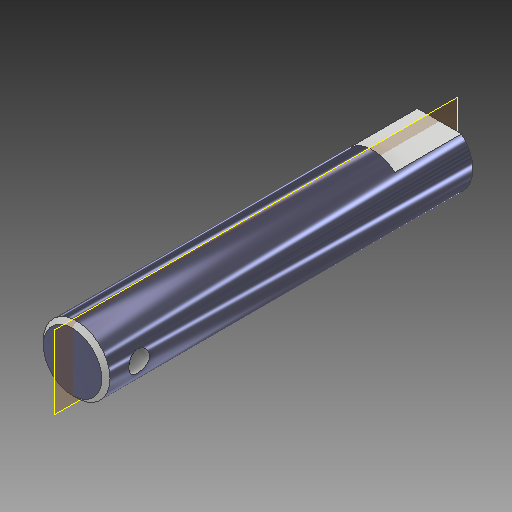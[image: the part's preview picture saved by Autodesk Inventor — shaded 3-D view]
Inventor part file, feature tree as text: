
AUTODESK INVENTOR PART (.ipt)
format: ipt  version: 2017 (Build 210142000, 142)  size: 155,648 bytes
history: native  units: mm
features: extrude x3, sketch x3, chamfer x1, plane x1
ambient origin geometry x8: Origin, YZ Plane, XZ Plane, XY Plane, X Axis, Y Axis, Z Axis, Center Point
bodies: Solid1 (feature_tree)
feature tree (8):
  extrude  "Extrusion1"  Depth=44.0mm TaperAngle=0.0deg
  chamfer  "Chamfer1"  Distance=0.5mm Angle=45.0deg
  extrude  "Extrusion2"  Depth=4.0mm
  plane  "Work Plane1"
  extrude  "Extrusion3"  Depth=4.0mm
  sketch  "Sketch2"  dims[d9=8.0mm d10=44.0mm d11=0.0mm d12=0.5mm d13=2.0mm d14=45.0deg]
  sketch  "Sketch3"  dims[d15=3.0mm d16=4.0mm]
  sketch  "Sketch4"  dims[d17=4.0mm d18=3.0mm d19=8.0mm d20=0.0mm d23=2.5mm d24=3.5mm d25=8.0mm d26=0.0mm]
